# Revit family: AA-14FB
name_source: partatom
category: Устройства связи
units: mm (PartAtom-declared; Revit-internal decimal feet)

## family parameters
Всегда вертикально = Нет
На основе рабочей плоскости = Да
Общий = Да
При загрузке вырезать с полостями = Нет
Размер круглого соединителя = Использовать диаметр
Сохранять ориентацию аннотаций = Нет
Тип детали = Нормальный
Точка принадлежности помещению = Нет

## types (1)
- AA-14FB
    ADSK_URL документации изделия = https://wiki.bas-ip.com
    ADSK_URL страницы изделия = https://www.bas-ip.ru
    ADSK_Версия Revit = Revit 2020
    ADSK_Единица измерения = шт.
    ADSK_Завод-изготовитель = BAS-IP
    ADSK_Классификация нагрузок = Вызывная панель
    ADSK_Количество фаз = 1
    ADSK_Марка = AA-14FB
    ADSK_Наименование = ВЫЗЫВНАЯ ПАНЕЛЬ AA-14FB
    ADSK_Напряжение = 12 В
    ADSK_Номинальная мощность = 7 Вт
    URL = https://www.bas-ip.ru
    Аутентификация = Отдельный пароль на настройки, WEB–интерфейс
    Выходное видео = HD (1920х1080), H.264 Main Profile
    Дисплей = 10, TFT, с подсветкой и подогревом
    Дополнительно = SIP P2P, встроенное реле, датчик приближения, открытый API, поддержка ПО Link
    Изготовитель = BAS-IP
    Изображение типоразмера = <Нет>
    Интеграция со СКУД = Выход WIEGAND-26, 32, 34, 37, 40, 42, 56, 58, 64 бит
    Интерфейс = Русский/английский, WEB–интерфейс
    Камера = 1/3”
    Класс степени защиты = IP65
    Кнопки быстрого вызова = Кнопка вызова консьержа
    Количество мелодий вызова = Свои загружаемые мелодии
    Контроль доступа = Мультиформатный считыватель с поддержкой технологии UKEY (EM-Marin, Mifare, Bluetooth, NFC)
    Корпус = Алюминий
    Минимальная освещенность = 0,01 LuX
    Ночная подсветка = 6 светодиодов
    Описание = Многоабонентская вызывная панель с 10“ TFT экраном с подсветкой и подогревом, с распознаванием лиц и поддержкой мобильного доступа BAS-IP UKEY
    Открытие замка = С монитора, по коду, по карте, из приложений BAS-IP Intercom, UKEY, распознавание по лицу
    Отметка по умолчанию = 0 мм
    Питание = +12 В
    Поддерживаемые аудиокодеки = G.711u
    Потребление питания = 6,5 Вт, в режиме ожидания – 3,6 Вт
    Размер под установку (кронштейна) = 172×378×58 мм
    Размер самой панели = 180×400×46 мм
    Разрешение камеры = 2 Мп
    Режим разговора = Двухсторонний
    Температурный режим = -40 ... +65 °С
    Тип клавиатуры = Сенсорная
    Тип панели = Многоквартирная
    Тип установки = Врезная
    Угол обзора = По горизонтали 90°, по вертикали 64°
    Цветовое решение = Золото, серебро, черный
